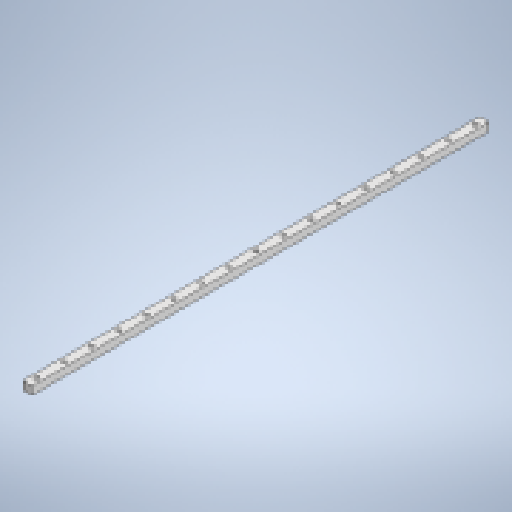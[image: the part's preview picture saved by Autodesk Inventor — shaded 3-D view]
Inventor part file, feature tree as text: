
AUTODESK INVENTOR PART (.ipt)
format: ipt  version: 2023 (Build 270158000, 158)  size: 181,248 bytes
history: native  units: mm
features: extrude x3, sketch x3, pattern_linear x1
ambient origin geometry x8: Origin, YZ Plane, XZ Plane, XY Plane, X Axis, Y Axis, Z Axis, Center Point
bodies: Solid1 (feature_tree)
feature tree (7):
  extrude  "Extrusion1"  Depth=17.5mm
  extrude  "Extrusion2"  Depth=1000.0mm
  extrude  "Extrusion3"  Depth=8.5mm TaperAngle=0.0deg
  pattern_linear  "Rectangular Pattern1"  Spacing1=9.5mm  [1 undecoded]
  sketch  "Sketch1"  dims[d0=20.0mm d1=17.5mm]
  sketch  "Sketch2"  dims[d2=1000.0mm d3=0.0mm d4=6.0mm]
  sketch  "Sketch3"  dims[d5=20.0mm d6=800.0mm d7=0.0mm d8=9.5mm d9=8.5mm d10=0.0mm d11=180.0mm d13=60.0mm]
note: 1 required parameter value undecoded (feature->parameter linkage not recoverable at this tier; creation-order binding heuristic only, values carry confidence <= 0.55)
